# Revit family: WAGNER_Угол_90.45
name_source: partatom
category: Соединительные детали трубопроводов
revit_build: Autodesk Revit 2017 (Build: 20190508_0315(x64)
units: mm (PartAtom-declared; Revit-internal decimal feet)

## family parameters
Всегда вертикально = Да
Заголовок OmniClass = Pipework Fittings
На основе рабочей плоскости = Нет
Номер OmniClass = 23.60.30.11.14
Общий = Да
При загрузке вырезать с полостями = Нет
Размер круглого соединителя = Использовать диаметр
Тип детали = Отвод

## types (4) — shared parameters
ADSK_URL документации изделия = https://ru.wagnergroup.com
ADSK_URL страницы изделия = https://ru.wagnergroup.com
ADSK_Версия Revit = Revit 2017
ADSK_Версия семейства = Версия 1
ADSK_Дата изменения = 18.07.20
ADSK_Единица измерения = шт.
ADSK_Завод-изготовитель = WAGNER
ADSK_Код изделия = -
COBie Category = Pipework Fittings
Masterformat Code = 22 01 10
Masterformat Title = Pipe and pumps
OmniClass Code = 23-27 43 15
OmniClass Title = Pipe Expansion Joints
UNSPSC Code = 40141720
UNSPSC Title = Plumbing connectors
URL = www.wagner-russia.com
Uniclass Code = Ac_10_40_63
Uniclass Title = Pipe fitting
WAGNER_Температурный режим. = от -20℃ до +60℃
bimon.ru = bimon.ru
Изготовитель = WAGNER
zero-valued in all types: ADSK_Размер_Высота, ADSK_Размер_Длина, ADSK_Размер_Ширина

## per-type parameters (varying)
| type | ADSK_Марка | ADSK_Материал | ADSK_Наименование | ADSK_Наименование краткое | WAGNER_Variation | WAGNER_Артикул | WAGNER_Название | WAGNER_Тип | Описание | угол |
| WAGNER_Угол_90_ABSR | Typ ABSR 2518-W90 | WAGNER_ABS | Угол 90 ABSR | Угол 90 ABSR | 3 | 01-10-9220 | Угол 90 ABSR | Typ ABSR 2518-W90 | Угол 90 ABSR | 90.00° |
| WAGNER_Угол_45_ABSR | Typ ABSR 2518-W45 | WAGNER_ABS | Угол 45 ABSR | Угол 45 ABSR | 4 | 01-10-9230 | Угол 45 ABSR | Typ ABSR 2518-W45 | Угол 45 ABSR | 45.00° |
| WAGNER_Угол_90_PVC | Typ 2519-W90 | WAGNER_PVC | Угол 90 PVC | Угол 90 PVC | 1 | 01-10-9020 | Угол 90 PVC | Typ 2519-W90 | Угол 90 PVC | 90.00° |
| WAGNER_Угол_45_PVC | Typ 2519-W45 | WAGNER_PVC | Угол 45 PVC | Угол 45 PVC | 2 | 01-10-9030 | Угол 45 PVC | Typ 2519-W45 | Угол 45 PVC | 45.00° |
